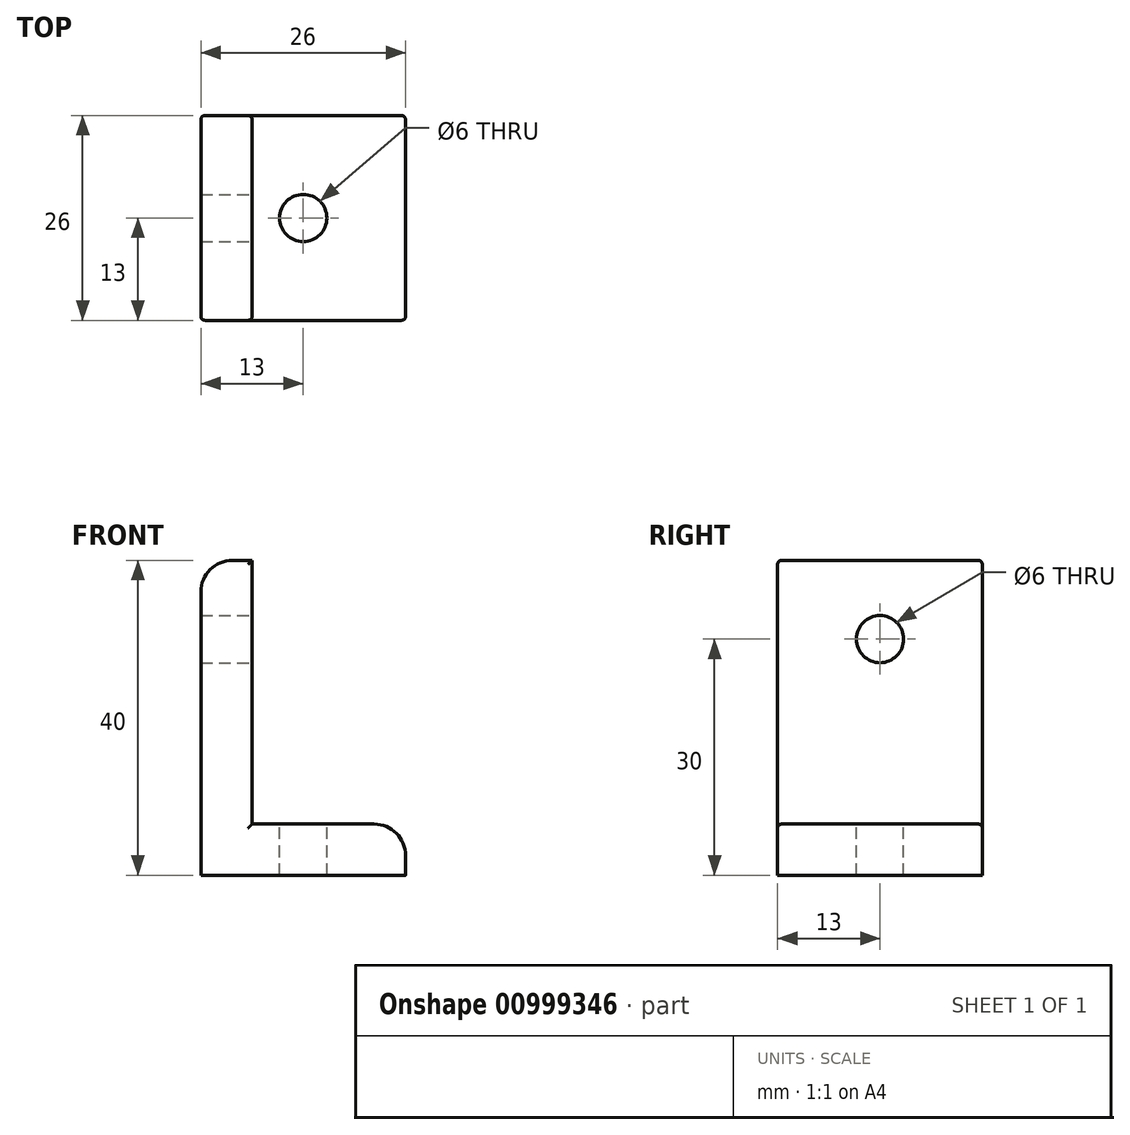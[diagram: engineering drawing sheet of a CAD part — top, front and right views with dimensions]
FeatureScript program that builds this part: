
annotation { "Feature Type Name" : "Feature", "Feature Type Description" : "" }
export const myFeature = defineFeature(function(context is Context, id is Id, definition is map)
    precondition{}
    {
        {
            var Q0;
            Q0=qCreatedBy(makeId("Front.planeOp"),FACE);
            var sketch = newSketch(context, id + "F0", { "sketchPlane" : qUnion([Q0])});
            skLineSegment(sketch, "E0", {"start": v(0, 33.5) * mm, "end": v(0, 0) * mm});
            skLineSegment(sketch, "E1", {"start": v(0, 0) * mm, "end": v(19.5, 0) * mm});
            skLineSegment(sketch, "E2", {"start": v(19.5, 0) * mm, "end": v(19.5, -6.5) * mm});
            skLineSegment(sketch, "E3", {"start": v(19.5, -6.5) * mm, "end": v(-6.5, -6.5) * mm});
            skLineSegment(sketch, "E4", {"start": v(-6.5, -6.5) * mm, "end": v(-6.5, 33.5) * mm});
            skLineSegment(sketch, "E5", {"start": v(-6.5, 33.5) * mm, "end": v(0, 33.5) * mm});
            skSolve(sketch);
        }
        {
            var Q0;
            Q0 = qSketchRegion(id + "F0", true);
            extrude(context, id + "F1", {"entities" : qUnion([Q0]), "oppositeDirection" : true, "depth" : 26 * mm, "offsetDistance" : 25 * mm});
        }
        {
            var Q0;
            Q0=qCreatedBy(makeId("Right.planeOp"),FACE);
            var sketch = newSketch(context, id + "F2", { "sketchPlane" : qUnion([Q0])});
            skCircle(sketch, "E6", {"center": v(13, 23.5) * mm, "radius": 3 * mm});
            skSolve(sketch);
        }
        {
            var Q0;
            Q0 = qSketchRegion(id + "F2", true);
            extrude(context, id + "F3", {"entities" : qUnion([Q0]), "operationType" : NewBodyOperationType.REMOVE, "oppositeDirection" : true, "depth" : 25 * mm, "offsetDistance" : 25 * mm});
        }
        {
            var Q0;
            Q0=qCreatedBy(makeId("Top.planeOp"),FACE);
            var sketch = newSketch(context, id + "F4", { "sketchPlane" : qUnion([Q0])});
            skCircle(sketch, "E7", {"center": v(6.5, 13) * mm, "radius": 3 * mm});
            skSolve(sketch);
        }
        {
            var Q0;
            Q0 = qSketchRegion(id + "F4", true);
            extrude(context, id + "F5", {"entities" : qUnion([Q0]), "operationType" : NewBodyOperationType.REMOVE, "oppositeDirection" : true, "depth" : 25 * mm, "offsetDistance" : 25 * mm});
        }
        {
            var Q0;
            Q0=makeQuery(id+"F1.opExtrude","SWEPT_EDGE",EDGE,{"disambiguationData":[OSD([sQuery(id+"F0.wireOp",EDGE,"E4"),sQuery(id+"F0.wireOp",EDGE,"E5")])]});
            var Q1;
            Q1=makeQuery(id+"F1.opExtrude","SWEPT_EDGE",EDGE,{"disambiguationData":[OSD([sQuery(id+"F0.wireOp",EDGE,"E1"),sQuery(id+"F0.wireOp",EDGE,"E2")])]});
            fillet(context, id + "F6", {"entities" : qUnion([Q0, Q1]), "radius" : 4 * mm, "tangentPropagation" : true, "allowEdgeOverflow" : false});
        }
        {
            var Q0;
            Q0=makeQuery(id+"F1.opExtrude","CAP_EDGE",EDGE,{"disambiguationData":[OSD([sQuery(id+"F0.wireOp",EDGE,"E4")])],"isStart":true});
            var Q1;
            Q1=makeQuery(id+"F1.opExtrude","CAP_EDGE",EDGE,{"disambiguationData":[OSD([sQuery(id+"F0.wireOp",EDGE,"E4")])],"isStart":false});
            var Q2;
            Q2=makeQuery(id+"F1.opExtrude","CAP_EDGE",EDGE,{"disambiguationData":[OSD([sQuery(id+"F0.wireOp",EDGE,"E1")])],"isStart":false});
            var Q3;
            Q3=makeQuery(id+"F1.opExtrude","CAP_EDGE",EDGE,{"disambiguationData":[OSD([sQuery(id+"F0.wireOp",EDGE,"E0")])],"isStart":false});
            var Q4;
            Q4=makeQuery(id+"F1.opExtrude","CAP_EDGE",EDGE,{"disambiguationData":[OSD([sQuery(id+"F0.wireOp",EDGE,"E0")])],"isStart":true});
            var Q5;
            Q5=makeQuery(id+"F1.opExtrude","CAP_EDGE",EDGE,{"disambiguationData":[OSD([sQuery(id+"F0.wireOp",EDGE,"E1")])],"isStart":true});
            fillet(context, id + "F7", {"entities" : qUnion([Q0, Q1, Q2, Q3, Q4, Q5]), "radius" : 0.5 * mm, "tangentPropagation" : true, "allowEdgeOverflow" : false});
        }
    });
